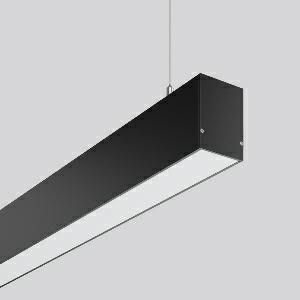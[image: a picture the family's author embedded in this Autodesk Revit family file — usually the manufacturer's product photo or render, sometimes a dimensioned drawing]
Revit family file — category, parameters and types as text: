
# Revit family: less_is_more_50_312311_003_1_76_4b1a
name_source: partatom
category: Lighting Fixtures
units: mm (PartAtom-declared; Revit-internal decimal feet)

## family parameters
Cut with Voids When Loaded = No
Host = Face
Light Source = No
Part Type = Normal
Room Calculation Point = No
Round Connector Dimension = Use Diameter
Shared = No

## types (1)
- LESS IS MORE 50 (1 x LED Modul 840, 2400 lm, 4000)
    Apparent Load = 22 VA
    CIE Flux Codes = 48 79 95 100 100
    Color Rendering = 80
    Color Temperature = 4000
    Default Elevation = 1800 mm
    Description = Series: LESS IS MORE 50
Linear pendant luminaire for aesthetically sophisticated lighting. Housing: extruded aluminium profile, powder-coated. End cap aluminium powder-coated. Canopy made of aluminium, powder-coated. Diffuser made of non-yellowing plastic (PMMA), opal. Direct light emission. Suitable for pendant. 2-point steel cable suspension freely positionable and infinitely height-adjustable. Special lengths available on request. LED unit with integrated converter interchangeable and removable. Suitable for through-wiring. With sensors or as a safety luminaire on request. 
Colour: deep black, matt (RAL 9005)
Length: 847 mm
Width: 57 mm
Height: 75 mm
Suspension length: 2000 mm
Lamp: LED
Socket: without socket
Colour temperature: 4000K
Colour rendering index (CRI): 80
System power: 22 W
Rated luminous flux: 2400 lm
Luminous efficiency: 109 lm/W
Control gear: Converter, dimmable, DALI
Protection class: I
Type of protection: IP 20
    Height = 75 mm
    Lamp = 1 x LED Modul 840
    Lamp Light Flux = 2400 lm
    Lamp count = 1
    Length = 847 mm
    Lifetime = 50000 h
    Luminous efficacy = 109 lm/W
    Manufacturer = RZB
    ModVariant = No
    Model = 312311.003.1.76
    Mounting Place = Ceiling
    Mounting Type = Pendant
    Number of Poles = 1
    OnlyDefault = Yes
    Power Factor = 1
    Product Name = LESS IS MORE 50
    Product group = Pendant LED linear luminaires
    ProductGroupID = 907
    Protection Class = Protection class I
    Protection Degree = IP 20
    RLX_Detail_Level = 1
    RLX_Emergency_Light_Flux = 0 lm
    RLX_Emergency_Type = 0
    RLX_Emergency_Type_DB = No
    RlxData = <blob elided: 28853 chars, md5=84d7b8b5>
    Socket = socket
    Standby Power = 0 W
    System Light Flux = 2400 lm
    System Power = 22 W
    Type Comments = Product without accessories
    Type Image = 312318.003.jpg
    URL = http://relux.com
    VarID = ---
    Voltage = 230 V
    Voltage Range = 220-240 V
    Weight = 0.00 kg
    Width = 57 mm

## geometry (parser evidence)
native form markers: Blend x4, Sweep x9
no freeform markers — native parametric forms only
